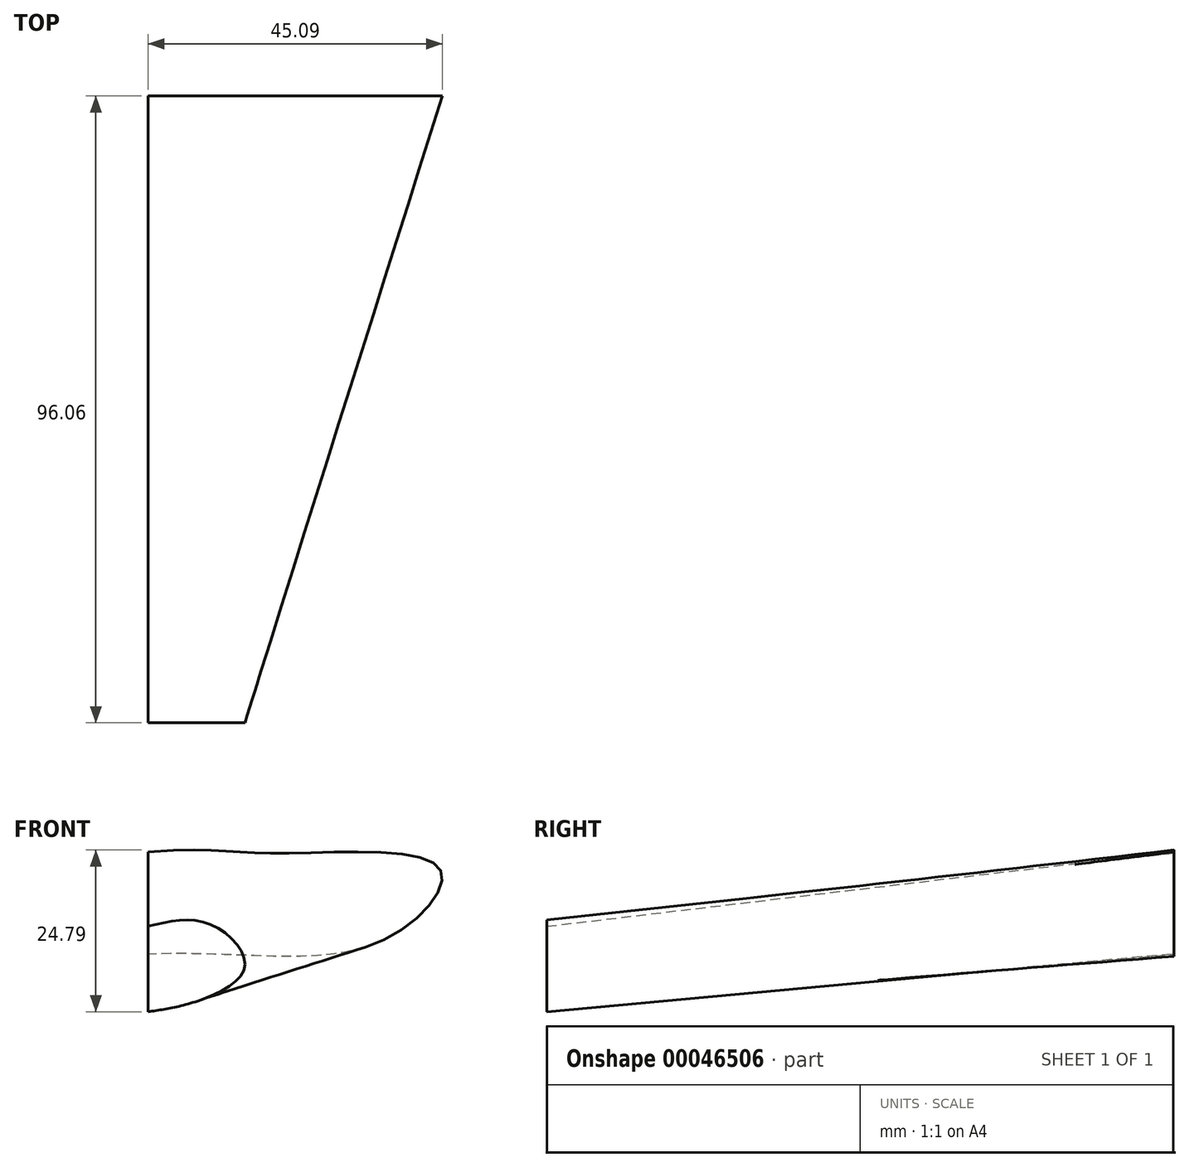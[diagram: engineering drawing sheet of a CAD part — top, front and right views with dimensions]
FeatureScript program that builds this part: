
annotation { "Feature Type Name" : "Feature", "Feature Type Description" : "" }
export const myFeature = defineFeature(function(context is Context, id is Id, definition is map)
    precondition{}
    {
        {
            var Q0;
            Q0=qCreatedBy(makeId("Right.planeOp"),FACE);
            var sketch = newSketch(context, id + "F0", { "sketchPlane" : qUnion([Q0])});
            skFitSpline(sketch, "E0", {"points": [v(-51.52, 17.73) * mm, v(-27.23, 23.32) * mm, v(7.4, 23.04) * mm, v(39.52, 27.79) * mm, v(44.54, 28.9) * mm], "startDerivative": vector(88.2, 27.84) * mm, "endDerivative": vector(32.02, 7.33) * mm});
            skSolve(sketch);
        }
        {
            var Q0;
            Q0=sQuery(id+"F0.wireOp",VERTEX,"E0.start");
            var Q1;
            Q1=qCreatedBy(makeId("Front.planeOp"),FACE);
            cPlane(context, id + "F1", {"entities" : qUnion([Q0, Q1]), "cplaneType" : CPlaneType.PLANE_POINT, "offset" : 152.4 * mm, "width" : 152.4 * mm, "height" : 152.4 * mm});
        }
        {
            var Q0;
            Q0=qCreatedBy(id+"F1.planeOp",FACE);
            var sketch = newSketch(context, id + "F2", { "sketchPlane" : qUnion([Q0])});
            skFitSpline(sketch, "E1", {"points": [v(0, 18.06) * mm, v(9.5, 18.38) * mm, v(14.8, 11.83) * mm, v(7.33, 6.53) * mm, v(0, 4.97) * mm], "startDerivative": vector(36.7, 8.97) * mm, "endDerivative": vector(-28.82, -4.02) * mm});
            skLineSegment(sketch, "E2", {"start": v(0, 18.06) * mm, "end": v(0, 4.97) * mm});
            skSolve(sketch);
        }
        {
            var Q0;
            Q0=sQuery(id+"F0.wireOp",VERTEX,"E0.4.internal");
            var Q1;
            Q1=qCreatedBy(makeId("Front.planeOp"),FACE);
            cPlane(context, id + "F3", {"entities" : qUnion([Q0, Q1]), "cplaneType" : CPlaneType.PLANE_POINT, "offset" : 152.4 * mm, "width" : 152.4 * mm, "height" : 152.4 * mm});
        }
        {
            var Q0;
            Q0=qCreatedBy(id+"F3.planeOp",FACE);
            var sketch = newSketch(context, id + "F4", { "sketchPlane" : qUnion([Q0])});
            skFitSpline(sketch, "E3", {"points": [v(0, 29.48) * mm, v(20.1, 29.24) * mm, v(44.69, 26.91) * mm, v(36.05, 15.95) * mm, v(0, 13.79) * mm], "startDerivative": vector(138.7, 9.68) * mm, "endDerivative": vector(-144.54, -5.96) * mm});
            skLineSegment(sketch, "E4", {"start": v(0, 29.48) * mm, "end": v(0, 13.79) * mm});
            skSolve(sketch);
        }
        {
            var Q0;
            Q0=makeQuery(id+"F2.imprint","IMPRINT",FACE,{"disambiguationData":[TD([[makeQuery(id+"F2.imprint","IMPRINT",EDGE,{"derivedFrom":sQuery(id+"F2.wireOp",EDGE,"E1")}),-1.0]])]});
            var Q1;
            Q1=makeQuery(id+"F4.imprint","IMPRINT",FACE,{"disambiguationData":[TD([[makeQuery(id+"F4.imprint","IMPRINT",EDGE,{"derivedFrom":sQuery(id+"F4.wireOp",EDGE,"E3")}),-1.0]])]});
            var Q2;
            Q2=sQuery(id+"F0.wireOp",EDGE,"E0");
            loft(context, id + "F5", {"sheetProfilesArray" : [{ "sheetProfileEntities" : qUnion([Q0]) }, { "sheetProfileEntities" : qUnion([Q1]) }], "guidesArray" : [{ "guideEntities" : qUnion([Q2]), "guideDerivativeType" : LoftGuideDerivativeType.DEFAULT, "guideDerivativeMagnitude" : 1 }]});
        }
    });
